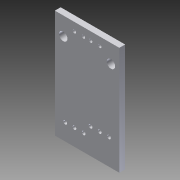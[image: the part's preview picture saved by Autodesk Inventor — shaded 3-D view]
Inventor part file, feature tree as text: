
AUTODESK INVENTOR PART (.ipt)
format: ipt  version: 2011 (Build 150239000, 239)  size: 84,480 bytes
history: native  units: in
note: dims shown in document units (in); Inventor stores cm internally (conversion verified against a paired STEP export)
features: extrude x1, imported_body x1
ambient origin geometry x8: Origin, YZ Plane, XZ Plane, XY Plane, X Axis, Y Axis, Z Axis, Center Point
feature tree (2):
  extrude  "Extrude3"  [1 undecoded]
  imported_body  "Base1"
note: 1 required parameter value undecoded (feature->parameter linkage not recoverable at this tier; creation-order binding heuristic only, values carry confidence <= 0.55)
